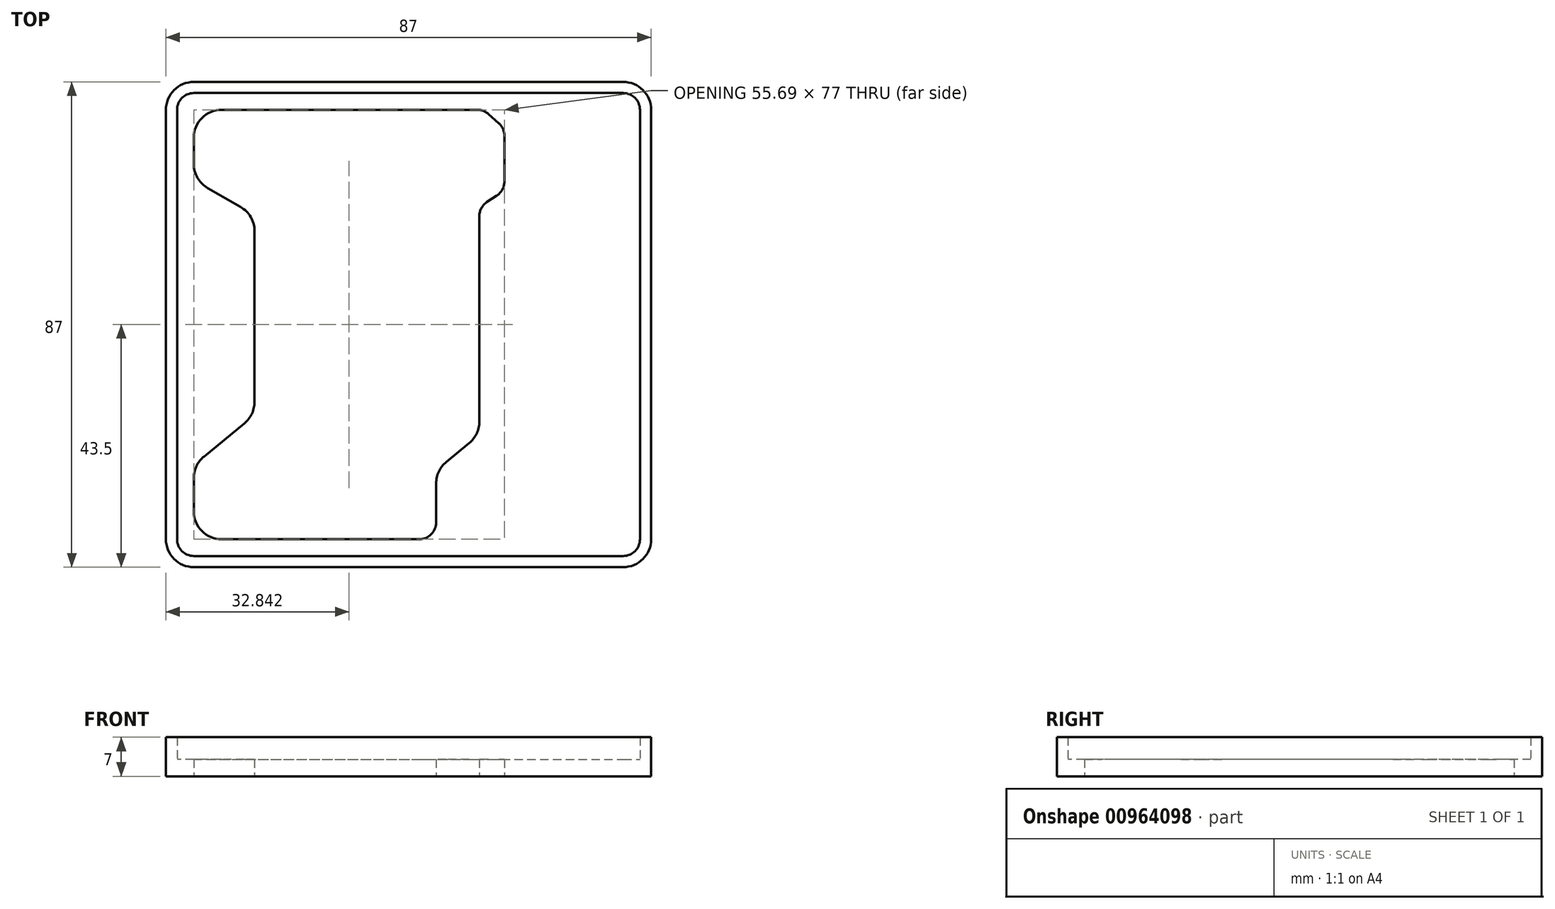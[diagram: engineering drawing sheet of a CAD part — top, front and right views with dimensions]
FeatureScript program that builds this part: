
annotation { "Feature Type Name" : "Feature", "Feature Type Description" : "" }
export const myFeature = defineFeature(function(context is Context, id is Id, definition is map)
    precondition{}
    {
        {
            var Q0;
            Q0=qCreatedBy(makeId("Top.planeOp"),FACE);
            var sketch = newSketch(context, id + "F0", { "sketchPlane" : qUnion([Q0])});
            skLineSegment(sketch, "E0.bottom", {"start": v(-43.45, 38.4) * mm, "end": v(33.55, 38.4) * mm});
            skLineSegment(sketch, "E0.top", {"start": v(-43.45, -48.6) * mm, "end": v(33.55, -48.6) * mm});
            skLineSegment(sketch, "E0.left", {"start": v(-48.45, 33.4) * mm, "end": v(-48.45, -43.6) * mm});
            skLineSegment(sketch, "E0.right", {"start": v(38.55, 33.4) * mm, "end": v(38.55, -43.6) * mm});
            skPoint(sketch, "E1.visualSharp", {"position": v(-48.45, 38.4) * mm});
            skArc(sketch, "E1.filletArc", {"start": v(-43.45, 38.4) * mm, "mid": v(-47, 36.94) * mm, "end": v(-48.45, 33.4) * mm});
            skPoint(sketch, "E2.visualSharp", {"position": v(38.55, 38.4) * mm});
            skArc(sketch, "E2.filletArc", {"start": v(38.55, 33.4) * mm, "mid": v(37.08, 36.94) * mm, "end": v(33.55, 38.4) * mm});
            skPoint(sketch, "E3.visualSharp", {"position": v(38.55, -48.6) * mm});
            skArc(sketch, "E3.filletArc", {"start": v(33.55, -48.6) * mm, "mid": v(37.08, -47.14) * mm, "end": v(38.55, -43.6) * mm});
            skPoint(sketch, "E4.visualSharp", {"position": v(-48.45, -48.6) * mm});
            skArc(sketch, "E4.filletArc", {"start": v(-48.45, -43.6) * mm, "mid": v(-47, -47.14) * mm, "end": v(-43.45, -48.6) * mm});
            skLineSegment(sketch, "E5.bottom", {"start": v(-43.45, 33.4) * mm, "end": v(-2.24, 33.4) * mm});
            skLineSegment(sketch, "E5.top", {"start": v(-43.45, -43.6) * mm, "end": v(-3, -43.6) * mm});
            skLineSegment(sketch, "E5.left", {"start": v(-43.45, 33.4) * mm, "end": v(-43.45, 23.7) * mm});
            skLineSegment(sketch, "E6", {"start": v(-40.94, 19.36) * mm, "end": v(-35.07, 16) * mm});
            skLineSegment(sketch, "E7", {"start": v(-32.56, 11.66) * mm, "end": v(-32.56, -18.94) * mm});
            skLineSegment(sketch, "E8", {"start": v(-34.39, -22.8) * mm, "end": v(-41.63, -28.76) * mm});
            skLineSegment(sketch, "E9.trimOffspring", {"start": v(-43.45, -32.62) * mm, "end": v(-43.45, -43.6) * mm});
            skLineSegment(sketch, "E10", {"start": v(7.74, 14.33) * mm, "end": v(7.74, -22.5) * mm});
            skLineSegment(sketch, "E11", {"start": v(5.92, -26.36) * mm, "end": v(1.82, -29.73) * mm});
            skLineSegment(sketch, "E12", {"start": v(0, -33.6) * mm, "end": v(0, -40.6) * mm});
            skPoint(sketch, "E13.visualSharp", {"position": v(-32.56, 14.55) * mm});
            skArc(sketch, "E13.filletArc", {"start": v(-32.56, 11.66) * mm, "mid": v(-33.23, 14.16) * mm, "end": v(-35.07, 16) * mm});
            skPoint(sketch, "E14.visualSharp", {"position": v(-32.56, -21.3) * mm});
            skArc(sketch, "E14.filletArc", {"start": v(-34.39, -22.8) * mm, "mid": v(-33.04, -21.08) * mm, "end": v(-32.56, -18.94) * mm});
            skPoint(sketch, "E15.visualSharp", {"position": v(0, -31.23) * mm});
            skArc(sketch, "E15.filletArc", {"start": v(1.82, -29.73) * mm, "mid": v(0.48, -31.46) * mm, "end": v(0, -33.6) * mm});
            skPoint(sketch, "E16.visualSharp", {"position": v(-43.45, -30.26) * mm});
            skArc(sketch, "E16.filletArc", {"start": v(-41.63, -28.76) * mm, "mid": v(-42.98, -30.49) * mm, "end": v(-43.45, -32.62) * mm});
            skPoint(sketch, "E17.visualSharp", {"position": v(7.74, -24.86) * mm});
            skArc(sketch, "E17.filletArc", {"start": v(5.92, -26.36) * mm, "mid": v(7.27, -24.64) * mm, "end": v(7.74, -22.5) * mm});
            skPoint(sketch, "E18.visualSharp", {"position": v(-43.45, 20.8) * mm});
            skArc(sketch, "E18.filletArc", {"start": v(-43.45, 23.7) * mm, "mid": v(-42.78, 21.2) * mm, "end": v(-40.94, 19.36) * mm});
            skLineSegment(sketch, "E19", {"start": v(9.1, 16.84) * mm, "end": v(10.88, 18.01) * mm});
            skLineSegment(sketch, "E20", {"start": v(12.24, 20.52) * mm, "end": v(12.24, 28.75) * mm});
            skLineSegment(sketch, "E21", {"start": v(0, 33.4) * mm, "end": v(7.4, 33.4) * mm});
            skLineSegment(sketch, "E22", {"start": v(9.41, 32.63) * mm, "end": v(11.24, 30.98) * mm});
            skLineSegment(sketch, "E23", {"start": v(-2.24, 33.4) * mm, "end": v(0, 33.4) * mm});
            skPoint(sketch, "E24.visualSharp", {"position": v(7.74, 15.95) * mm});
            skArc(sketch, "E24.filletArc", {"start": v(9.1, 16.84) * mm, "mid": v(8.1, 15.76) * mm, "end": v(7.74, 14.33) * mm});
            skPoint(sketch, "E25.visualSharp", {"position": v(12.24, 18.9) * mm});
            skArc(sketch, "E25.filletArc", {"start": v(10.88, 18.01) * mm, "mid": v(11.88, 19.1) * mm, "end": v(12.24, 20.52) * mm});
            skPoint(sketch, "E26.visualSharp", {"position": v(12.24, 30.09) * mm});
            skArc(sketch, "E26.filletArc", {"start": v(12.24, 28.75) * mm, "mid": v(11.98, 29.97) * mm, "end": v(11.24, 30.98) * mm});
            skPoint(sketch, "E27.visualSharp", {"position": v(8.56, 33.4) * mm});
            skArc(sketch, "E27.filletArc", {"start": v(9.41, 32.63) * mm, "mid": v(8.48, 33.2) * mm, "end": v(7.4, 33.4) * mm});
            skPoint(sketch, "E28.visualSharp", {"position": v(0, -43.6) * mm});
            skArc(sketch, "E28.filletArc", {"start": v(-3, -43.6) * mm, "mid": v(-0.88, -42.72) * mm, "end": v(0, -40.6) * mm});
            skSolve(sketch);
        }
        {
            var Q0;
            Q0=makeQuery(id+"F0.imprint","IMPRINT",FACE,{"disambiguationData":[TD([[makeQuery(id+"F0.imprint","IMPRINT",EDGE,{"derivedFrom":sQuery(id+"F0.wireOp",EDGE,"E0.bottom")}),-1.0]])]});
            extrude(context, id + "F1", {"entities" : qUnion([Q0]), "depth" : 3 * mm, "offsetDistance" : 25 * mm});
        }
        {
            var Q0;
            Q0=makeQuery(id+"F1.opExtrude","SWEPT_EDGE",EDGE,{"disambiguationData":[OSD([sQuery(id+"F0.wireOp",EDGE,"E5.bottom"),sQuery(id+"F0.wireOp",EDGE,"E5.left")])]});
            fillet(context, id + "F2", {"entities" : qUnion([Q0]), "radius" : 5 * mm, "tangentPropagation" : true, "allowEdgeOverflow" : false});
        }
        {
            var Q0;
            Q0=makeQuery(id+"F1.opExtrude","SWEPT_EDGE",EDGE,{"disambiguationData":[OSD([sQuery(id+"F0.wireOp",EDGE,"E5.top"),sQuery(id+"F0.wireOp",EDGE,"E9.trimOffspring")])]});
            fillet(context, id + "F3", {"entities" : qUnion([Q0]), "radius" : 5 * mm, "tangentPropagation" : true, "allowEdgeOverflow" : false});
        }
        {
            var Q0;
            Q0=makeQuery(id+"F1.opExtrude","CAP_FACE",FACE,{"disambiguationData":[OSD([sQuery(id+"F0.wireOp",EDGE,"E0.bottom"),sQuery(id+"F0.wireOp",EDGE,"E0.top"),sQuery(id+"F0.wireOp",EDGE,"E0.left"),sQuery(id+"F0.wireOp",EDGE,"E0.right"),sQuery(id+"F0.wireOp",EDGE,"E1.filletArc"),sQuery(id+"F0.wireOp",EDGE,"E2.filletArc"),sQuery(id+"F0.wireOp",EDGE,"E3.filletArc"),sQuery(id+"F0.wireOp",EDGE,"E4.filletArc"),sQuery(id+"F0.wireOp",EDGE,"E5.bottom"),sQuery(id+"F0.wireOp",EDGE,"E5.top"),sQuery(id+"F0.wireOp",EDGE,"E5.left"),sQuery(id+"F0.wireOp",EDGE,"E6"),sQuery(id+"F0.wireOp",EDGE,"E7"),sQuery(id+"F0.wireOp",EDGE,"E8"),sQuery(id+"F0.wireOp",EDGE,"E9.trimOffspring"),sQuery(id+"F0.wireOp",EDGE,"E10"),sQuery(id+"F0.wireOp",EDGE,"E11"),sQuery(id+"F0.wireOp",EDGE,"E12"),sQuery(id+"F0.wireOp",EDGE,"E13.filletArc"),sQuery(id+"F0.wireOp",EDGE,"E14.filletArc"),sQuery(id+"F0.wireOp",EDGE,"E15.filletArc"),sQuery(id+"F0.wireOp",EDGE,"E16.filletArc"),sQuery(id+"F0.wireOp",EDGE,"E17.filletArc"),sQuery(id+"F0.wireOp",EDGE,"E18.filletArc"),sQuery(id+"F0.wireOp",EDGE,"E19"),sQuery(id+"F0.wireOp",EDGE,"E20"),sQuery(id+"F0.wireOp",EDGE,"E21"),sQuery(id+"F0.wireOp",EDGE,"E22"),sQuery(id+"F0.wireOp",EDGE,"E23"),sQuery(id+"F0.wireOp",EDGE,"E24.filletArc"),sQuery(id+"F0.wireOp",EDGE,"E25.filletArc"),sQuery(id+"F0.wireOp",EDGE,"E26.filletArc"),sQuery(id+"F0.wireOp",EDGE,"E27.filletArc"),sQuery(id+"F0.wireOp",EDGE,"E28.filletArc")])],"isStart":false});
            var sketch = newSketch(context, id + "F4", { "sketchPlane" : qUnion([Q0])});
            skLineSegment(sketch, "E29.bottom", {"start": v(-43.45, 38.4) * mm, "end": v(33.55, 38.4) * mm});
            skLineSegment(sketch, "E29.top", {"start": v(-43.45, -48.6) * mm, "end": v(33.55, -48.6) * mm});
            skLineSegment(sketch, "E29.left", {"start": v(-48.45, 33.4) * mm, "end": v(-48.45, -43.6) * mm});
            skLineSegment(sketch, "E29.right", {"start": v(38.55, 33.4) * mm, "end": v(38.55, -43.6) * mm});
            skArc(sketch, "E30.filletArc", {"start": v(-43.45, 38.4) * mm, "mid": v(-47, 36.94) * mm, "end": v(-48.45, 33.4) * mm});
            skPoint(sketch, "E31.visualSharp", {"position": v(38.55, 38.4) * mm});
            skArc(sketch, "E31.filletArc", {"start": v(38.55, 33.4) * mm, "mid": v(37.08, 36.94) * mm, "end": v(33.55, 38.4) * mm});
            skArc(sketch, "E32.filletArc", {"start": v(33.55, -48.6) * mm, "mid": v(37.08, -47.14) * mm, "end": v(38.55, -43.6) * mm});
            skArc(sketch, "E33.filletArc", {"start": v(-48.45, -43.6) * mm, "mid": v(-47, -47.14) * mm, "end": v(-43.45, -48.6) * mm});
            skArc(sketch, "E34.0", {"start": v(-43.45, 36.4) * mm, "mid": v(-45.58, 35.52) * mm, "end": v(-46.45, 33.4) * mm});
            skLineSegment(sketch, "E34.1", {"start": v(-46.45, 33.4) * mm, "end": v(-46.45, -43.6) * mm});
            skLineSegment(sketch, "E34.2", {"start": v(-43.45, 36.4) * mm, "end": v(33.55, 36.4) * mm});
            skArc(sketch, "E34.3", {"start": v(-46.45, -43.6) * mm, "mid": v(-45.58, -45.72) * mm, "end": v(-43.45, -46.6) * mm});
            skArc(sketch, "E34.4", {"start": v(36.55, 33.4) * mm, "mid": v(35.67, 35.52) * mm, "end": v(33.55, 36.4) * mm});
            skLineSegment(sketch, "E34.5", {"start": v(36.55, 33.4) * mm, "end": v(36.55, -43.6) * mm});
            skArc(sketch, "E34.6", {"start": v(33.55, -46.6) * mm, "mid": v(35.67, -45.72) * mm, "end": v(36.55, -43.6) * mm});
            skLineSegment(sketch, "E34.7", {"start": v(-43.45, -46.6) * mm, "end": v(33.55, -46.6) * mm});
            skSolve(sketch);
        }
        {
            var Q0;
            Q0=makeQuery(id+"F4.imprint","IMPRINT",FACE,{"disambiguationData":[TD([[makeQuery(id+"F4.imprint","IMPRINT",EDGE,{"derivedFrom":sQuery(id+"F4.wireOp",EDGE,"E29.bottom")}),-1.0]])]});
            extrude(context, id + "F5", {"entities" : qUnion([Q0]), "operationType" : NewBodyOperationType.ADD, "depth" : 4 * mm, "offsetDistance" : 25 * mm});
        }
    });
